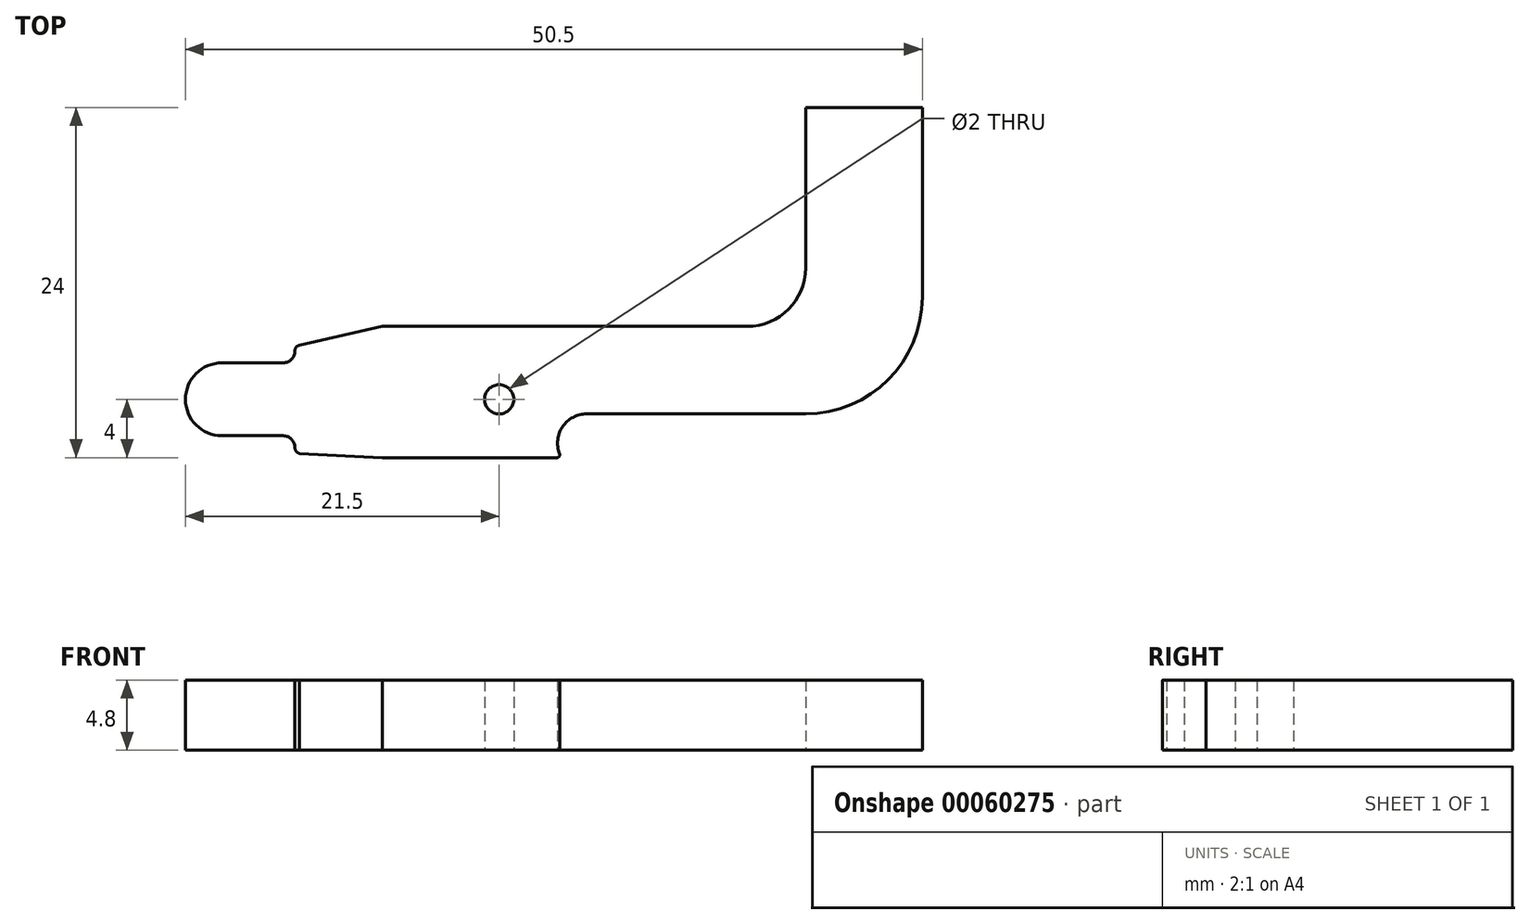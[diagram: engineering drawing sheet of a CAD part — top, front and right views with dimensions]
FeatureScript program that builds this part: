
annotation { "Feature Type Name" : "Feature", "Feature Type Description" : "" }
export const myFeature = defineFeature(function(context is Context, id is Id, definition is map)
    precondition{}
    {
        {
            var Q0;
            Q0=qCreatedBy(makeId("Top.planeOp"),FACE);
            var sketch = newSketch(context, id + "F0", { "sketchPlane" : qUnion([Q0])});
            skLineSegment(sketch, "E0", {"start": v(48, 12) * mm, "end": v(48, 25) * mm});
            skLineSegment(sketch, "E1", {"start": v(48, 25) * mm, "end": v(40, 25) * mm});
            skLineSegment(sketch, "E2", {"start": v(40, 25) * mm, "end": v(40, 14) * mm});
            skLineSegment(sketch, "E3", {"start": v(36, 10) * mm, "end": v(11, 10) * mm});
            skPoint(sketch, "E4.visualSharp", {"position": v(48, 0) * mm});
            skPoint(sketch, "E5.visualSharp", {"position": v(40, 10) * mm});
            skArc(sketch, "E5.filletArc", {"start": v(36, 10) * mm, "mid": v(38.83, 11.17) * mm, "end": v(40, 14) * mm});
            skLineSegment(sketch, "E6", {"start": v(48, 15) * mm, "end": v(19, 15) * mm, "construction": true});
            skLineSegment(sketch, "E7", {"start": v(19, 15) * mm, "end": v(19, -7.71) * mm, "construction": true});
            skLineSegment(sketch, "E8", {"start": v(0, 5) * mm, "end": v(54.82, 5) * mm, "construction": true});
            skCircle(sketch, "E9", {"center": v(19, 5) * mm, "radius": 1 * mm});
            skArc(sketch, "E10", {"start": v(0, 7.5) * mm, "mid": v(-2.5, 5) * mm, "end": v(0, 2.5) * mm});
            skLineSegment(sketch, "E11", {"start": v(11, -2.16) * mm, "end": v(11, 16.4) * mm, "construction": true});
            skLineSegment(sketch, "E12", {"start": v(5.31, 8.7) * mm, "end": v(11, 10) * mm});
            skPoint(sketch, "E13.orphan", {"position": v(0, 0) * mm});
            skPoint(sketch, "E14.orphan", {"position": v(0, 10) * mm});
            skLineSegment(sketch, "E15", {"start": v(25, 15) * mm, "end": v(25, -7.92) * mm, "construction": true});
            skLineSegment(sketch, "E16", {"start": v(25, 4) * mm, "end": v(40, 4) * mm});
            skArc(sketch, "E17", {"start": v(25, 4) * mm, "mid": v(23.35, 3.13) * mm, "end": v(23.14, 1.27) * mm});
            skPoint(sketch, "E17.endSnap0", {"position": v(25, 3.54) * mm});
            skPoint(sketch, "E18.visualSharp", {"position": v(25, 0) * mm});
            skArc(sketch, "E19.filletArc", {"start": v(40, 4) * mm, "mid": v(45.66, 6.34) * mm, "end": v(48, 12) * mm});
            skLineSegment(sketch, "E20", {"start": v(5, 14.19) * mm, "end": v(5, -5.44) * mm, "construction": true});
            skLineSegment(sketch, "E21", {"start": v(0, 2.5) * mm, "end": v(4.2, 2.5) * mm});
            skLineSegment(sketch, "E22", {"start": v(0, 7.5) * mm, "end": v(4.2, 7.5) * mm});
            skLineSegment(sketch, "E23", {"start": v(5, 8.3) * mm, "end": v(5, 8.32) * mm});
            skLineSegment(sketch, "E24", {"start": v(5, 1.7) * mm, "end": v(5, 1.68) * mm});
            skPoint(sketch, "E25.visualSharp", {"position": v(5, 7.5) * mm});
            skArc(sketch, "E25.filletArc", {"start": v(4.2, 7.5) * mm, "mid": v(4.77, 7.73) * mm, "end": v(5, 8.3) * mm});
            skPoint(sketch, "E26.visualSharp", {"position": v(5, 2.5) * mm});
            skArc(sketch, "E26.filletArc", {"start": v(5, 1.7) * mm, "mid": v(4.77, 2.27) * mm, "end": v(4.2, 2.5) * mm});
            skPoint(sketch, "E27.visualSharp", {"position": v(5, 1.36) * mm});
            skArc(sketch, "E27.filletArc", {"start": v(5, 1.68) * mm, "mid": v(5.09, 1.43) * mm, "end": v(5.31, 1.3) * mm});
            skPoint(sketch, "E28.visualSharp", {"position": v(5, 8.64) * mm});
            skArc(sketch, "E28.filletArc", {"start": v(5.31, 8.7) * mm, "mid": v(5.09, 8.57) * mm, "end": v(5, 8.32) * mm});
            skLineSegment(sketch, "E29.0", {"start": v(11, 1) * mm, "end": v(22.95, 1) * mm});
            skLineSegment(sketch, "E30", {"start": v(5.31, 1.3) * mm, "end": v(11, 1) * mm});
            skPoint(sketch, "E31.visualSharp", {"position": v(23.27, 1) * mm});
            skArc(sketch, "E31.filletArc", {"start": v(22.95, 1) * mm, "mid": v(23.12, 1.09) * mm, "end": v(23.14, 1.27) * mm});
            skSolve(sketch);
        }
        {
            var Q0;
            Q0=makeQuery(id+"F0.imprint","IMPRINT",FACE,{"disambiguationData":[TD([[makeQuery(id+"F0.imprint","IMPRINT",EDGE,{"derivedFrom":sQuery(id+"F0.wireOp",EDGE,"E0")}),1.0]])]});
            extrude(context, id + "F1", {"entities" : qUnion([Q0]), "depth" : 4.8 * mm});
        }
    });
